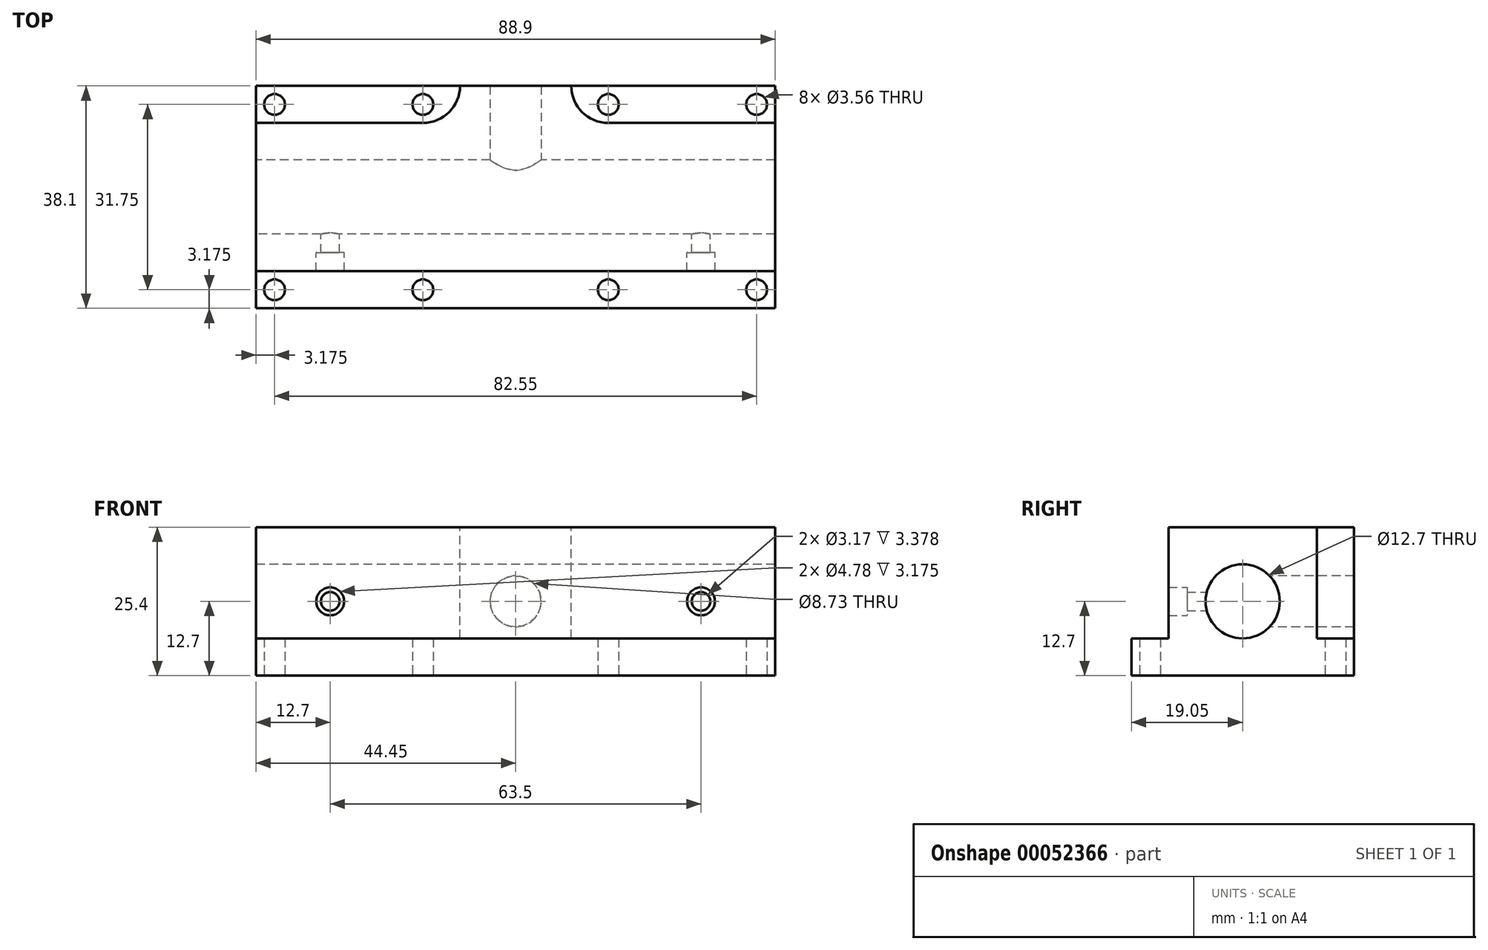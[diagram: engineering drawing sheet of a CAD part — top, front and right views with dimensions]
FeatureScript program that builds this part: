
annotation { "Feature Type Name" : "Feature", "Feature Type Description" : "" }
export const myFeature = defineFeature(function(context is Context, id is Id, definition is map)
    precondition{}
    {
        {
            var Q0;
            Q0=qCreatedBy(makeId("Right.planeOp"),FACE);
            var sketch = newSketch(context, id + "F0", { "sketchPlane" : qUnion([Q0])});
            skLineSegment(sketch, "E0.bottom", {"start": v(-19.05, -12.7) * mm, "end": v(19.05, -12.7) * mm});
            skLineSegment(sketch, "E0.top", {"start": v(-19.05, 12.7) * mm, "end": v(19.05, 12.7) * mm});
            skLineSegment(sketch, "E0.left", {"start": v(-19.05, -12.7) * mm, "end": v(-19.05, 12.7) * mm});
            skLineSegment(sketch, "E0.right", {"start": v(19.05, -12.7) * mm, "end": v(19.05, 12.7) * mm});
            skPoint(sketch, "E1", {"position": v(0, 12.7) * mm});
            skPoint(sketch, "E2", {"position": v(19.05, 0) * mm});
            skCircle(sketch, "E3", {"center": v(0, 0) * mm, "radius": 6.35 * mm});
            skSolve(sketch);
        }
        {
            var Q0;
            Q0 = qSketchRegion(id + "F0", true);
            extrude(context, id + "F1", {"entities" : qUnion([Q0]), "depth" : 88.9 * mm, "symmetric" : true});
        }
        {
            var Q0;
            Q0=makeQuery(id+"F1.opExtrude","SWEPT_FACE",FACE,{"disambiguationData":[OSD([sQuery(id+"F0.wireOp",EDGE,"E0.top")])]});
            var sketch = newSketch(context, id + "F2", { "sketchPlane" : qUnion([Q0])});
            skLineSegment(sketch, "E4.bottom", {"start": v(-44.45, 19.05) * mm, "end": v(-9.53, 19.05) * mm});
            skLineSegment(sketch, "E4.top", {"start": v(-44.45, 12.7) * mm, "end": v(-15.87, 12.7) * mm});
            skLineSegment(sketch, "E4.left", {"start": v(-44.45, 19.05) * mm, "end": v(-44.45, 12.7) * mm});
            skLineSegment(sketch, "E4.right", {"start": v(44.45, 19.05) * mm, "end": v(44.45, 12.7) * mm});
            skLineSegment(sketch, "E5.bottom", {"start": v(-44.45, -19.05) * mm, "end": v(44.45, -19.05) * mm});
            skLineSegment(sketch, "E5.top", {"start": v(-44.45, -12.7) * mm, "end": v(44.45, -12.7) * mm});
            skLineSegment(sketch, "E5.left", {"start": v(-44.45, -19.05) * mm, "end": v(-44.45, -12.7) * mm});
            skLineSegment(sketch, "E5.right", {"start": v(44.45, -19.05) * mm, "end": v(44.45, -12.7) * mm});
            skLineSegment(sketch, "E6.trimOffspring", {"start": v(15.87, 12.7) * mm, "end": v(44.45, 12.7) * mm});
            skLineSegment(sketch, "E7.trimOffspring", {"start": v(9.52, 19.05) * mm, "end": v(44.45, 19.05) * mm});
            skArc(sketch, "E8", {"start": v(-9.52, 19.05) * mm, "mid": v(-11.38, 14.56) * mm, "end": v(-15.87, 12.7) * mm});
            skArc(sketch, "E9", {"start": v(9.52, 19.05) * mm, "mid": v(11.38, 14.56) * mm, "end": v(15.87, 12.7) * mm});
            skSolve(sketch);
        }
        {
            var Q0;
            Q0 = qSketchRegion(id + "F2", true);
            extrude(context, id + "F3", {"entities" : qUnion([Q0]), "operationType" : NewBodyOperationType.REMOVE, "oppositeDirection" : true, "depth" : 19.05 * mm});
        }
        {
            var Q0;
            Q0=makeQuery(id+"F1.opExtrude","SWEPT_FACE",FACE,{"disambiguationData":[OSD([sQuery(id+"F0.wireOp",EDGE,"E0.right")])]});
            var sketch = newSketch(context, id + "F4", { "sketchPlane" : qUnion([Q0])});
            skPoint(sketch, "E10", {"position": v(0, 0) * mm});
            skSolve(sketch);
        }
        {
            var Q0;
            Q0=sQuery(id+"F4.wireOp",VERTEX,"E10");
            var Q1;
            Q1=makeQuery(id+"F1.opExtrude","SWEPT_BODY",BODY,{"disambiguationData":[OSD([sQuery(id+"F0.wireOp",EDGE,"E0.bottom"),sQuery(id+"F0.wireOp",EDGE,"E0.top"),sQuery(id+"F0.wireOp",EDGE,"E0.left"),sQuery(id+"F0.wireOp",EDGE,"E0.right"),sQuery(id+"F0.wireOp",EDGE,"E3")])]});
            hole(context, id + "F5", {"style" : HoleStyle.SIMPLE, "holeDiameter" : 8.73 * mm, "endStyle" : HoleEndStyle.BLIND, "holeDepth" : 19.05 * mm, "locations" : qUnion([Q0]), "scope" : qUnion([Q1])});
        }
        {
            var Q0;
            Q0=makeQuery(id+"F3.boolean.opBoolean","COPY",FACE,{"derivedFrom":makeQuery(id+"F3.opExtrude","SWEPT_FACE",FACE,{"disambiguationData":[OSD([sQuery(id+"F2.wireOp",EDGE,"E5.top")])]})});
            var sketch = newSketch(context, id + "F6", { "sketchPlane" : qUnion([Q0])});
            skPoint(sketch, "E11", {"position": v(-31.75, 0) * mm});
            skPoint(sketch, "E12", {"position": v(31.75, 0) * mm});
            skSolve(sketch);
        }
        {
            var Q0;
            Q0=sQuery(id+"F6.wireOp",VERTEX,"E11");
            var Q1;
            Q1=sQuery(id+"F6.wireOp",VERTEX,"E12");
            var Q2;
            Q2=makeQuery(id+"F1.opExtrude","SWEPT_BODY",BODY,{"disambiguationData":[OSD([sQuery(id+"F0.wireOp",EDGE,"E0.bottom"),sQuery(id+"F0.wireOp",EDGE,"E0.top"),sQuery(id+"F0.wireOp",EDGE,"E0.left"),sQuery(id+"F0.wireOp",EDGE,"E0.right"),sQuery(id+"F0.wireOp",EDGE,"E3")])]});
            hole(context, id + "F7", {"style" : HoleStyle.C_BORE, "holeDiameter" : 3.17 * mm, "cBoreDiameter" : 4.78 * mm, "cBoreDepth" : 3.17 * mm, "endStyle" : HoleEndStyle.BLIND, "holeDepth" : 12.7 * mm, "locations" : qUnion([Q0, Q1]), "scope" : qUnion([Q2])});
        }
        {
            var Q0;
            Q0=makeQuery(id+"F3.boolean.opBoolean","COPY",FACE,{"derivedFrom":makeQuery(id+"F3.opExtrude","CAP_FACE",FACE,{"disambiguationData":[OSD([sQuery(id+"F2.wireOp",EDGE,"E5.bottom"),sQuery(id+"F2.wireOp",EDGE,"E5.top"),sQuery(id+"F2.wireOp",EDGE,"E5.left"),sQuery(id+"F2.wireOp",EDGE,"E5.right")])],"isStart":false})});
            var sketch = newSketch(context, id + "F8", { "sketchPlane" : qUnion([Q0])});
            skPoint(sketch, "E13", {"position": v(-41.28, 15.88) * mm});
            skPoint(sketch, "E14", {"position": v(-15.88, 15.88) * mm});
            skPoint(sketch, "E15", {"position": v(15.87, 15.88) * mm});
            skPoint(sketch, "E16", {"position": v(41.27, 15.88) * mm});
            skPoint(sketch, "E17", {"position": v(-41.28, -15.88) * mm});
            skPoint(sketch, "E18", {"position": v(-15.88, -15.88) * mm});
            skPoint(sketch, "E19", {"position": v(15.87, -15.88) * mm});
            skPoint(sketch, "E20", {"position": v(41.27, -15.88) * mm});
            skSolve(sketch);
        }
        {
            var Q0;
            Q0=sQuery(id+"F8.wireOp",VERTEX,"E13");
            var Q1;
            Q1=sQuery(id+"F8.wireOp",VERTEX,"E14");
            var Q2;
            Q2=sQuery(id+"F8.wireOp",VERTEX,"E15");
            var Q3;
            Q3=sQuery(id+"F8.wireOp",VERTEX,"E16");
            var Q4;
            Q4=sQuery(id+"F8.wireOp",VERTEX,"E20");
            var Q5;
            Q5=sQuery(id+"F8.wireOp",VERTEX,"E19");
            var Q6;
            Q6=sQuery(id+"F8.wireOp",VERTEX,"E18");
            var Q7;
            Q7=sQuery(id+"F8.wireOp",VERTEX,"E17");
            var Q8;
            Q8=makeQuery(id+"F1.opExtrude","SWEPT_BODY",BODY,{"disambiguationData":[OSD([sQuery(id+"F0.wireOp",EDGE,"E0.bottom"),sQuery(id+"F0.wireOp",EDGE,"E0.top"),sQuery(id+"F0.wireOp",EDGE,"E0.left"),sQuery(id+"F0.wireOp",EDGE,"E0.right"),sQuery(id+"F0.wireOp",EDGE,"E3")])]});
            hole(context, id + "F9", {"style" : HoleStyle.SIMPLE, "holeDiameter" : 3.56 * mm, "endStyle" : HoleEndStyle.THROUGH, "locations" : qUnion([Q0, Q1, Q2, Q3, Q4, Q5, Q6, Q7]), "scope" : qUnion([Q8])});
        }
    });
